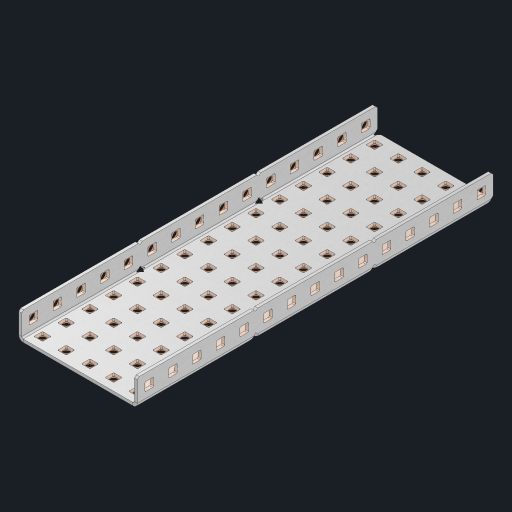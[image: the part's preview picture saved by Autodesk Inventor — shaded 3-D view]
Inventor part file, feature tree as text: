
AUTODESK INVENTOR PART (.ipt)
format: ipt  version: 2023 (Build 270158000, 158)  size: 1,350,144 bytes
history: native  units: in
note: dims shown in document units (in); Inventor stores cm internally (conversion verified against a paired STEP export)
features: other x110, extrude x104, sheet_metal_op x10, sketch x8, mirror x1, pattern_linear x1, chamfer x1
ambient origin geometry x8: Origin, YZ Plane, XZ Plane, XY Plane, X Axis, Y Axis, Z Axis, Center Point
bodies: Solid1 (feature_tree), Body (feature_tree)
feature tree (235):
  other  "Flange Pattern Plane"
  sheet_metal_op  "Flange Pattern"
  sheet_metal_op  "Body Pattern"
  other  "Arc Length"
  mirror  "Notch Mirror"
  pattern_linear  "Notch Pattern"  Spacing1=0.25in  [1 undecoded]
  chamfer  "End Chamfer"
  extrude  "Half Cut"  Depth=0.0625in
  sketch  "Sketch1"  dims[d0=2.5in]
  other  "Plate1"
  sketch  "Sketch2"  dims[d1=7.5in]
  other  "Plate2"
  sheet_metal_op  "Bend1"
  sheet_metal_op  "Corner1"
  sketch  "Sketch3"  dims[d2=0.0625in]
  other  "Flange Pattern Sketch"
  sketch  "Sketch7"  dims[d3=0.0625in]
  other  "Srf1"
  other  "Srf2"
  sketch  "Sketch8"  dims[d4=0.0312in]
  sketch  "Sketch9"  dims[d5=0.125in]
  other  "Srf91"
  sheet_metal_op  "Body Pattern Sketch"
  other  "Srf92"
  sketch  "Sketch13"  dims[d6=0.0625in]
  sketch  "Sketch14"  dims[d7=0.5in d8=90.0deg d9=0.0312in d10=0.25in d11=0.0625in d12=0.0625in d16=0.182in d17=0.02in d18=0.0625in d19=0.0in d20=0.25in d21=0.25in d46=0.172in d47=1.0in d48=0.0in d49=0.182in d50=0.02in d51=0.25in d52=0.25in d53=0.0625in d54=0.0in d55=0.172in d56=1.0in d57=0.0in d60=5.9055in d62=0.5in d63=1.9685in d65=0.5in d85=0.1473in d86=0.1782in d88=0.04in d89=0.0625in d90=0.0in d91=0.04in d92=0.0491in d95=2.5in d96=0.04in d97=0.25in d98=45.0deg d101=0.0in d102=2.497in d131=2.5in d132=5.9055in d134=0.5in d139=0.5in]
  other  "Srf856"
  other  "Srf1310"
  other  "Srf1311"
  other  "Srf1312"
  other  "Srf1376"
  other  "Srf1377"
  other  "Srf1728"
  other  "Srf1755"
  other  "Srf1878"
  other  "Srf1879"
  other  "Srf1880"
  other  "Srf1881"
  other  "Srf1882"
  other  "Srf1883"
  other  "Srf1884"
  other  "Srf1885"
  other  "Srf1886"
  other  "Srf1887"
  other  "Srf1888"
  other  "Srf1889"
  other  "Srf1890"
  other  "Srf1891"
  other  "Srf1892"
  other  "Srf1893"
  other  "Srf1894"
  other  "Srf1895"
  other  "Srf1896"
  other  "Srf1897"
  other  "Srf1898"
  other  "Srf1899"
  other  "Srf1900"
  other  "Srf1901"
  other  "Srf1942"
  other  "Srf1943"
  other  "Srf1944"
  other  "Srf1945"
  other  "Srf1946"
  other  "Srf1947"
  other  "Srf1948"
  other  "Srf1949"
  other  "Srf1950"
  other  "Srf1951"
  other  "Srf1952"
  other  "Srf1953"
  other  "Srf1954"
  other  "Srf1955"
  other  "Srf1956"
  other  "Srf1957"
  other  "Srf1958"
  other  "Srf1959"
  other  "Srf1960"
  other  "Srf1961"
  other  "Srf1962"
  other  "Srf1963"
  other  "Srf1964"
  other  "Srf1965"
  other  "Srf1966"
  other  "Srf1967"
  other  "Srf1968"
  other  "Srf1969"
  other  "Srf1970"
  other  "Srf2146"
  other  "Srf2147"
  other  "Srf2148"
  other  "Srf2149"
  other  "Srf2150"
  other  "Srf2151"
  other  "Srf2152"
  other  "Srf2153"
  other  "Srf2154"
  other  "Srf2155"
  other  "Srf2156"
  other  "Srf2157"
  other  "Srf2158"
  other  "Srf2159"
  other  "Srf2160"
  other  "Srf2161"
  other  "Srf2162"
  other  "Srf2163"
  other  "Srf2164"
  other  "Srf2165"
  other  "Srf2166"
  other  "Srf2167"
  other  "Srf2168"
  other  "Srf2169"
  other  "Srf2170"
  other  "Srf2171"
  other  "Srf2172"
  other  "Srf2173"
  other  "Srf2174"
  other  "Srf2175"
  other  "Srf2176"
  other  "Srf2177"
  other  "Srf2178"
  other  "Srf2179"
  other  "Srf2180"
  other  "Srf2181"
  other  "Srf2182"
  other  "Srf2183"
  other  "Srf2184"
  other  "Srf2185"
  sheet_metal_op  "Flange Stamp"
  sheet_metal_op  "Flange Circle"
  sheet_metal_op  "Body Stamp"
  sheet_metal_op  "Body Circle"
  sheet_metal_op  "Notch"
  extrude  "ExtrusionSrf2"  Depth=0.0625in
  extrude  "ExtrusionSrf92"  Depth=2.5in
  extrude  "ExtrusionSrf856"  Depth=0.02in
  extrude  "ExtrusionSrf1310"  Depth=0.0625in
  extrude  "ExtrusionSrf1311"  TaperAngle=0.0deg  [1 undecoded]
  extrude  "ExtrusionSrf1312"  Depth=0.25in
  extrude  "ExtrusionSrf1376"  Depth=0.25in
  extrude  "ExtrusionSrf1377"  Depth=2.5in
  extrude  "ExtrusionSrf1728"  Depth=2.5in TaperAngle=0.0deg
  extrude  "ExtrusionSrf1755"  Depth=2.5in
  extrude  "ExtrusionSrf1878"  Depth=0.02in
  extrude  "ExtrusionSrf1879"  Depth=0.25in
  extrude  "ExtrusionSrf1880"  Depth=0.25in
  extrude  "ExtrusionSrf1881"  Depth=0.0625in
  extrude  "ExtrusionSrf1882"  TaperAngle=0.0deg  [1 undecoded]
  extrude  "ExtrusionSrf1883"  Depth=2.5in
  extrude  "ExtrusionSrf1884"  Depth=2.5in TaperAngle=0.0deg
  extrude  "ExtrusionSrf1885"  Depth=2.5in
  extrude  "ExtrusionSrf1886"  Depth=2.5in
  extrude  "ExtrusionSrf1887"  Depth=2.5in
  extrude  "ExtrusionSrf1888"  Depth=2.5in
  extrude  "ExtrusionSrf1889"  Depth=2.5in
  extrude  "ExtrusionSrf1890"  Depth=0.0625in
  extrude  "ExtrusionSrf1891"  TaperAngle=0.0deg  [1 undecoded]
  extrude  "ExtrusionSrf1892"  Depth=2.5in
  extrude  "ExtrusionSrf1893"  Depth=2.5in
  extrude  "ExtrusionSrf1894"  Depth=2.5in
  extrude  "ExtrusionSrf1895"  Depth=0.25in TaperAngle=45.0deg
  extrude  "ExtrusionSrf1896"  TaperAngle=0.0deg  [1 undecoded]
  extrude  "ExtrusionSrf1897"  Depth=2.5in
  extrude  "ExtrusionSrf1898"  Depth=2.5in
  extrude  "ExtrusionSrf1899"  Depth=2.5in
  extrude  "ExtrusionSrf1900"  Depth=2.5in
  extrude  "ExtrusionSrf1901"  Depth=2.5in
  extrude  "ExtrusionSrf1942"  [1 undecoded]
  extrude  "ExtrusionSrf1943"  [1 undecoded]
  extrude  "ExtrusionSrf1944"  [1 undecoded]
  extrude  "ExtrusionSrf1945"  [1 undecoded]
  extrude  "ExtrusionSrf1946"  [1 undecoded]
  extrude  "ExtrusionSrf1947"  [1 undecoded]
  extrude  "ExtrusionSrf1948"  [1 undecoded]
  extrude  "ExtrusionSrf1949"  [1 undecoded]
  extrude  "ExtrusionSrf1950"  [1 undecoded]
  extrude  "ExtrusionSrf1951"  [1 undecoded]
  extrude  "ExtrusionSrf1952"  [1 undecoded]
  extrude  "ExtrusionSrf1953"  [1 undecoded]
  extrude  "ExtrusionSrf1954"  [1 undecoded]
  extrude  "ExtrusionSrf1955"  [1 undecoded]
  extrude  "ExtrusionSrf1956"  [1 undecoded]
  extrude  "ExtrusionSrf1957"  [1 undecoded]
  extrude  "ExtrusionSrf1958"  [1 undecoded]
  extrude  "ExtrusionSrf1959"  [1 undecoded]
  extrude  "ExtrusionSrf1960"  [1 undecoded]
  extrude  "ExtrusionSrf1961"  [1 undecoded]
  extrude  "ExtrusionSrf1962"  [1 undecoded]
  extrude  "ExtrusionSrf1963"  [1 undecoded]
  extrude  "ExtrusionSrf1964"  [1 undecoded]
  extrude  "ExtrusionSrf1965"  [1 undecoded]
  extrude  "ExtrusionSrf1966"  [1 undecoded]
  extrude  "ExtrusionSrf1967"  [1 undecoded]
  extrude  "ExtrusionSrf1968"  [1 undecoded]
  extrude  "ExtrusionSrf1969"  [1 undecoded]
  extrude  "ExtrusionSrf1970"  [1 undecoded]
  extrude  "ExtrusionSrf2146"  [1 undecoded]
  extrude  "ExtrusionSrf2147"  [1 undecoded]
  extrude  "ExtrusionSrf2148"  [1 undecoded]
  extrude  "ExtrusionSrf2149"  [1 undecoded]
  extrude  "ExtrusionSrf2150"  [1 undecoded]
  extrude  "ExtrusionSrf2151"  [1 undecoded]
  extrude  "ExtrusionSrf2152"  [1 undecoded]
  extrude  "ExtrusionSrf2153"  [1 undecoded]
  extrude  "ExtrusionSrf2154"  [1 undecoded]
  extrude  "ExtrusionSrf2155"  [1 undecoded]
  extrude  "ExtrusionSrf2156"  [1 undecoded]
  extrude  "ExtrusionSrf2157"  [1 undecoded]
  extrude  "ExtrusionSrf2158"  [1 undecoded]
  extrude  "ExtrusionSrf2159"  [1 undecoded]
  extrude  "ExtrusionSrf2160"  [1 undecoded]
  extrude  "ExtrusionSrf2161"  [1 undecoded]
  extrude  "ExtrusionSrf2162"  [1 undecoded]
  extrude  "ExtrusionSrf2163"  [1 undecoded]
  extrude  "ExtrusionSrf2164"  [1 undecoded]
  extrude  "ExtrusionSrf2165"  [1 undecoded]
  extrude  "ExtrusionSrf2166"  [1 undecoded]
  extrude  "ExtrusionSrf2167"  [1 undecoded]
  extrude  "ExtrusionSrf2168"  [1 undecoded]
  extrude  "ExtrusionSrf2169"  [1 undecoded]
  extrude  "ExtrusionSrf2170"  [1 undecoded]
  extrude  "ExtrusionSrf2171"  [1 undecoded]
  extrude  "ExtrusionSrf2172"  [1 undecoded]
  extrude  "ExtrusionSrf2173"  [1 undecoded]
  extrude  "ExtrusionSrf2174"  [1 undecoded]
  extrude  "ExtrusionSrf2175"  [1 undecoded]
  extrude  "ExtrusionSrf2176"  [1 undecoded]
  extrude  "ExtrusionSrf2177"  [1 undecoded]
  extrude  "ExtrusionSrf2178"  [1 undecoded]
  extrude  "ExtrusionSrf2179"  [1 undecoded]
  extrude  "ExtrusionSrf2180"  [1 undecoded]
  extrude  "ExtrusionSrf2181"  [1 undecoded]
  extrude  "ExtrusionSrf2182"  [1 undecoded]
  extrude  "ExtrusionSrf2183"  [1 undecoded]
  extrude  "ExtrusionSrf2184"  [1 undecoded]
  extrude  "ExtrusionSrf2185"  [1 undecoded]
note: 74 required parameter values undecoded (feature->parameter linkage not recoverable at this tier; creation-order binding heuristic only, values carry confidence <= 0.55)
